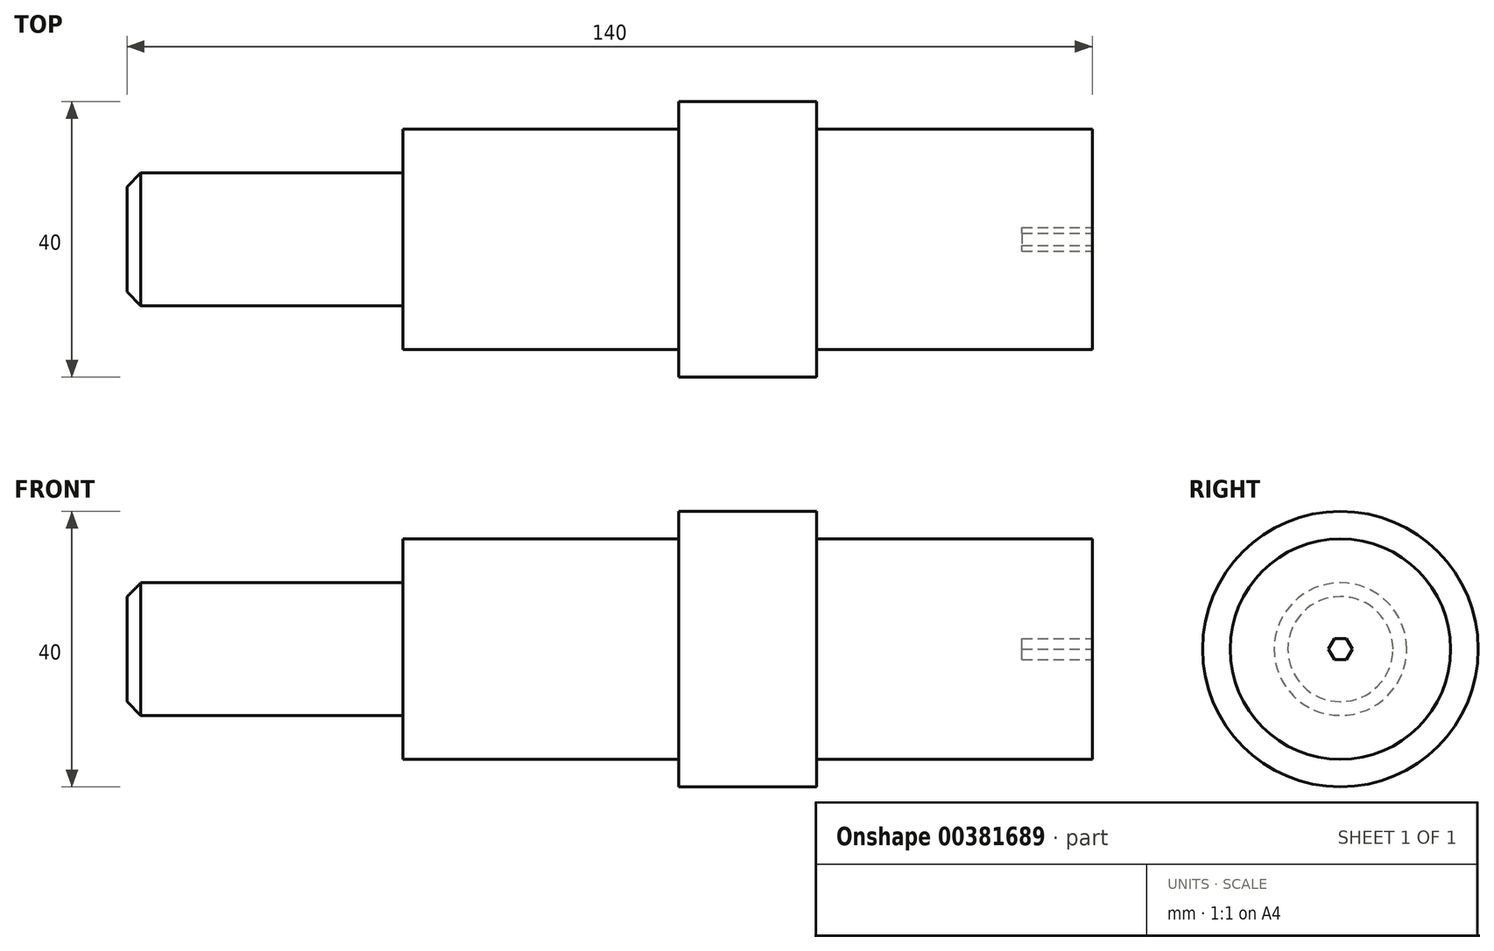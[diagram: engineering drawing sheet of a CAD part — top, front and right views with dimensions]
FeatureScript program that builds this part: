
annotation { "Feature Type Name" : "Feature", "Feature Type Description" : "" }
export const myFeature = defineFeature(function(context is Context, id is Id, definition is map)
    precondition{}
    {
        {
            var Q0;
            Q0=qCreatedBy(makeId("Right.planeOp"),FACE);
            var sketch = newSketch(context, id + "F0", { "sketchPlane" : qUnion([Q0])});
            skCircle(sketch, "E0", {"center": v(0, 0) * mm, "radius": 20 * mm});
            skSolve(sketch);
        }
        {
            var Q0;
            Q0 = qSketchRegion(id + "F0", true);
            extrude(context, id + "F1", {"entities" : qUnion([Q0]), "oppositeDirection" : true, "depth" : 20 * mm});
        }
        {
            var Q0;
            Q0=makeQuery(id+"F1.opExtrude","CAP_FACE",FACE,{"disambiguationData":[OSD([sQuery(id+"F0.wireOp",EDGE,"E0")])],"isStart":false});
            var sketch = newSketch(context, id + "F2", { "sketchPlane" : qUnion([Q0])});
            skCircle(sketch, "E1", {"center": v(0, 0) * mm, "radius": 16 * mm});
            skSolve(sketch);
        }
        {
            var Q0;
            Q0 = qSketchRegion(id + "F2", true);
            extrude(context, id + "F3", {"entities" : qUnion([Q0]), "operationType" : NewBodyOperationType.ADD, "depth" : 40 * mm});
        }
        {
            var Q0;
            Q0=makeQuery(id+"F3.opExtrude","CAP_FACE",FACE,{"disambiguationData":[OSD([sQuery(id+"F2.wireOp",EDGE,"E1")])],"isStart":false});
            var sketch = newSketch(context, id + "F4", { "sketchPlane" : qUnion([Q0])});
            skCircle(sketch, "E2", {"center": v(0, 0) * mm, "radius": 9.63 * mm});
            skSolve(sketch);
        }
        {
            var Q0;
            Q0 = qSketchRegion(id + "F4", true);
            extrude(context, id + "F5", {"entities" : qUnion([Q0]), "operationType" : NewBodyOperationType.ADD, "depth" : 40 * mm});
        }
        {
            var Q0;
            Q0=makeQuery(id+"F5.opExtrude","CAP_EDGE",EDGE,{"disambiguationData":[OSD([sQuery(id+"F4.wireOp",EDGE,"E2")])],"isStart":false});
            chamfer(context, id + "F6", {"entities" : qUnion([Q0]), "width" : 2 * mm, "tangentPropagation" : true});
        }
        {
            var Q0;
            Q0=makeQuery(id+"F1.opExtrude","CAP_FACE",FACE,{"disambiguationData":[OSD([sQuery(id+"F0.wireOp",EDGE,"E0")])],"isStart":true});
            var sketch = newSketch(context, id + "F7", { "sketchPlane" : qUnion([Q0])});
            skCircle(sketch, "E3", {"center": v(0, 0) * mm, "radius": 16 * mm});
            skSolve(sketch);
        }
        {
            var Q0;
            Q0 = qSketchRegion(id + "F7", true);
            extrude(context, id + "F8", {"entities" : qUnion([Q0]), "operationType" : NewBodyOperationType.ADD, "depth" : 40 * mm});
        }
        {
            var Q0;
            Q0=makeQuery(id+"F8.opExtrude","CAP_FACE",FACE,{"disambiguationData":[OSD([sQuery(id+"F7.wireOp",EDGE,"E3")])],"isStart":false});
            var sketch = newSketch(context, id + "F9", { "sketchPlane" : qUnion([Q0])});
            skLineSegment(sketch, "E4", {"start": v(0, 0) * mm, "end": v(-3.72, 0) * mm, "construction": true});
            skLineSegment(sketch, "E5", {"start": v(0.87, -1.5) * mm, "end": v(-0.87, -1.5) * mm});
            skLineSegment(sketch, "E6", {"start": v(0.87, 1.5) * mm, "end": v(-0.87, 1.5) * mm});
            skCircle(sketch, "E7", {"center": v(0, 0) * mm, "radius": 1.5 * mm, "construction": true});
            skLineSegment(sketch, "E8", {"start": v(1.73, 0) * mm, "end": v(0.87, 1.5) * mm});
            skLineSegment(sketch, "E9", {"start": v(-0.87, -1.5) * mm, "end": v(-1.73, 0) * mm});
            skLineSegment(sketch, "E10.trimOffspring", {"start": v(0.87, -1.5) * mm, "end": v(1.73, 0) * mm});
            skLineSegment(sketch, "E11.trimOffspring", {"start": v(-1.73, 0) * mm, "end": v(-0.87, 1.5) * mm});
            skSolve(sketch);
        }
        {
            var Q0;
            Q0 = qSketchRegion(id + "F9", true);
            extrude(context, id + "F10", {"entities" : qUnion([Q0]), "operationType" : NewBodyOperationType.REMOVE, "oppositeDirection" : true, "depth" : 10.2 * mm});
        }
    });
